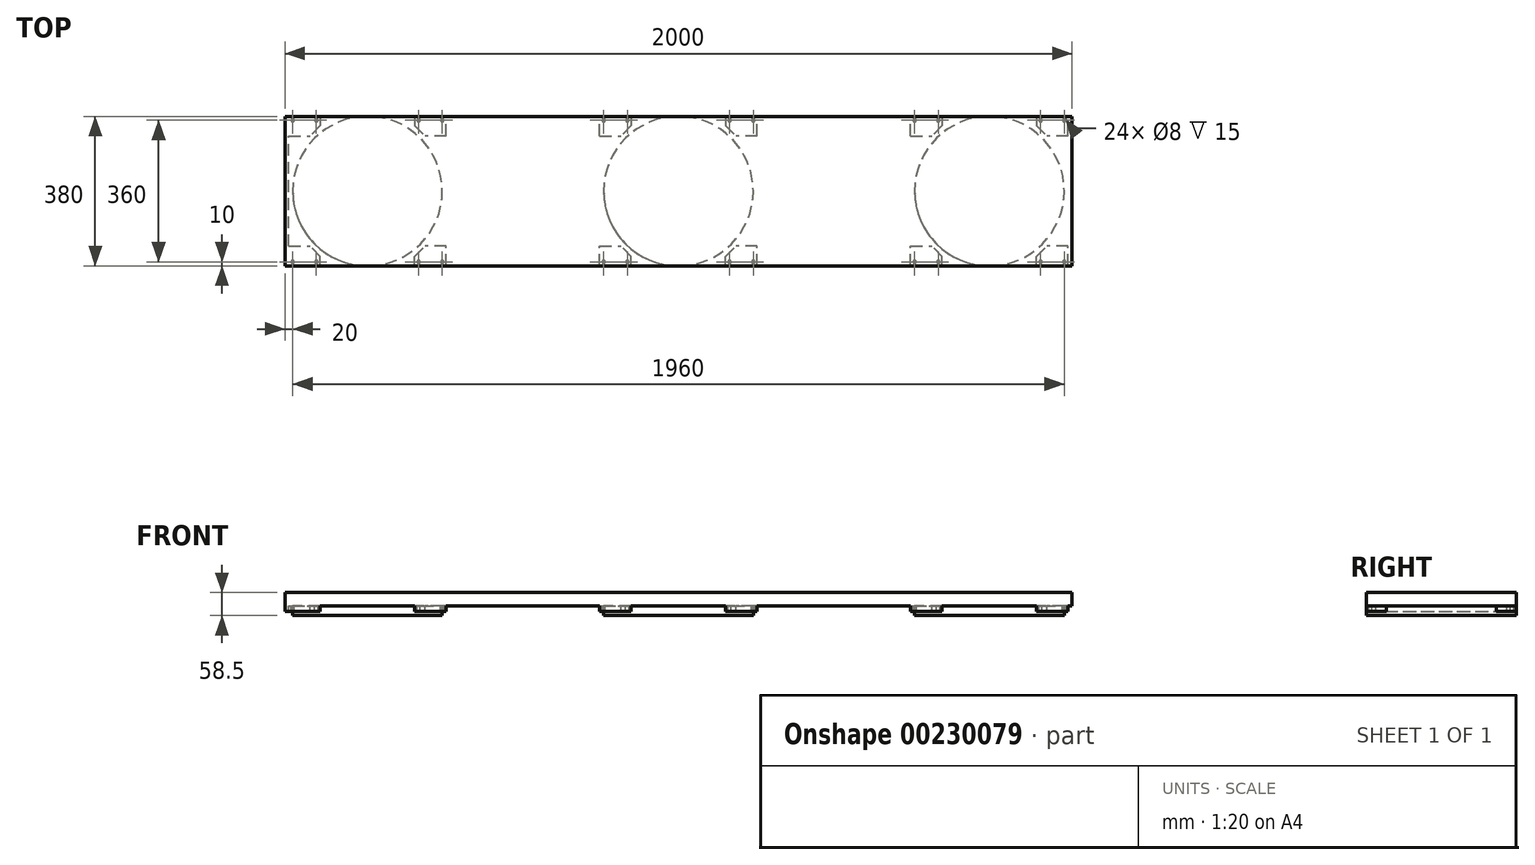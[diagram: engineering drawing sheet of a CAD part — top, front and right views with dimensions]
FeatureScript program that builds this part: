
annotation { "Feature Type Name" : "Feature", "Feature Type Description" : "" }
export const myFeature = defineFeature(function(context is Context, id is Id, definition is map)
    precondition{}
    {
        {
            var Q0;
            Q0=qCreatedBy(makeId("Right.planeOp"),FACE);
            var sketch = newSketch(context, id + "F0", { "sketchPlane" : qUnion([Q0])});
            skLineSegment(sketch, "E0.bottom", {"start": v(-190, 0) * mm, "end": v(190, 0) * mm});
            skLineSegment(sketch, "E0.top", {"start": v(-190, 33.5) * mm, "end": v(190, 33.5) * mm});
            skLineSegment(sketch, "E0.left", {"start": v(-190, 0) * mm, "end": v(-190, 33.5) * mm});
            skLineSegment(sketch, "E0.right", {"start": v(190, 0) * mm, "end": v(190, 33.5) * mm});
            skSolve(sketch);
        }
        {
            var Q0;
            Q0=makeQuery(id+"F0.imprint","IMPRINT",FACE,{"disambiguationData":[TD([[makeQuery(id+"F0.imprint","IMPRINT",EDGE,{"derivedFrom":sQuery(id+"F0.wireOp",EDGE,"E0.bottom")}),1.0]])]});
            extrude(context, id + "F1", {"entities" : qUnion([Q0]), "endBound" : BoundingType.SYMMETRIC, "depth" : 2000 * mm});
        }
        {
            var Q0;
            Q0=makeQuery(id+"F1.opExtrude","SWEPT_FACE",FACE,{"disambiguationData":[OSD([sQuery(id+"F0.wireOp",EDGE,"E0.bottom")])]});
            var sketch = newSketch(context, id + "F2", { "sketchPlane" : qUnion([Q0])});
            skCircle(sketch, "E1", {"center": v(-790, 0) * mm, "radius": 190 * mm});
            skCircle(sketch, "E2", {"center": v(0, 0) * mm, "radius": 190 * mm});
            skCircle(sketch, "E3", {"center": v(790, 0) * mm, "radius": 190 * mm});
            skLineSegment(sketch, "E4", {"start": v(-790, 0) * mm, "end": v(-790, 348.57) * mm, "construction": true});
            skSolve(sketch);
        }
        {
            var Q0;
            Q0=makeQuery(id+"F2.imprint","IMPRINT",FACE,{"disambiguationData":[TD([[makeQuery(id+"F2.imprint","IMPRINT",EDGE,{"derivedFrom":sQuery(id+"F2.wireOp",EDGE,"E1")}),1.0]])]});
            var Q1;
            Q1=makeQuery(id+"F2.imprint","IMPRINT",FACE,{"disambiguationData":[TD([[makeQuery(id+"F2.imprint","IMPRINT",EDGE,{"derivedFrom":sQuery(id+"F2.wireOp",EDGE,"E2")}),1.0]])]});
            var Q2;
            Q2=makeQuery(id+"F2.imprint","IMPRINT",FACE,{"disambiguationData":[TD([[makeQuery(id+"F2.imprint","IMPRINT",EDGE,{"derivedFrom":sQuery(id+"F2.wireOp",EDGE,"E3")}),1.0]])]});
            extrude(context, id + "F3", {"entities" : qUnion([Q0, Q1, Q2]), "operationType" : NewBodyOperationType.ADD, "depth" : 25 * mm});
        }
        {
            var Q0;
            {var subQ1=sQuery(id+"F0.wireOp",EDGE,"E0.left");var subQ3=sQuery(id+"F0.wireOp",EDGE,"E0.bottom");Q0=makeQuery(id+"F3.boolean.opBoolean","SPLIT",FACE,{"disambiguationData":[TD([makeQuery(id+"F1.opExtrude","SWEPT_FACE",FACE,{"disambiguationData":[OSD([subQ1])]})])],"derivedFrom":makeQuery(id+"F1.opExtrude","SWEPT_FACE",FACE,{"disambiguationData":[OSD([subQ3])]})});}
            var sketch = newSketch(context, id + "F4", { "sketchPlane" : qUnion([Q0])});
            skLineSegment(sketch, "E5", {"start": v(-1000, 190) * mm, "end": v(-1000, 70) * mm});
            skLineSegment(sketch, "E6.MirrorCS", {"start": v(1000, 190) * mm, "end": v(1000, 70) * mm});
            skLineSegment(sketch, "E7.MirrorCS", {"start": v(1000, -70) * mm, "end": v(1000, -195) * mm});
            skLineSegment(sketch, "E8", {"start": v(-1000, 70) * mm, "end": v(1000, 70) * mm, "construction": true});
            skLineSegment(sketch, "E9", {"start": v(1000, -70) * mm, "end": v(-1000, -70) * mm, "construction": true});
            skLineSegment(sketch, "E10", {"start": v(-990, 190) * mm, "end": v(-990, -190) * mm});
            skLineSegment(sketch, "E11.MirrorCS", {"start": v(990, 190) * mm, "end": v(990, -190) * mm});
            skLineSegment(sketch, "E12.bottom", {"start": v(-990, 190) * mm, "end": v(-910, 190) * mm});
            skLineSegment(sketch, "E12.top", {"start": v(-990, 140) * mm, "end": v(-935.72, 140) * mm});
            skLineSegment(sketch, "E12.left", {"start": v(-990, 190) * mm, "end": v(-990, 140) * mm});
            skLineSegment(sketch, "E12.right", {"start": v(-910, 190) * mm, "end": v(-910, 166.15) * mm});
            skLineSegment(sketch, "E13", {"start": v(-910, 166.15) * mm, "end": v(-935.72, 140) * mm});
            skLineSegment(sketch, "E14.MirrorCS", {"start": v(-990, -140) * mm, "end": v(-935.72, -140) * mm});
            skLineSegment(sketch, "E15.MirrorCS", {"start": v(-910, -166.15) * mm, "end": v(-935.72, -140) * mm});
            skLineSegment(sketch, "E16.MirrorCS", {"start": v(-910, -190) * mm, "end": v(-910, -166.15) * mm});
            skLineSegment(sketch, "E17.MirrorCS", {"start": v(-990, -190) * mm, "end": v(-910, -190) * mm});
            skLineSegment(sketch, "E18.MirrorCS", {"start": v(990, 140) * mm, "end": v(935.72, 140) * mm});
            skLineSegment(sketch, "E19.MirrorCS", {"start": v(910, 166.15) * mm, "end": v(935.72, 140) * mm});
            skLineSegment(sketch, "E20.MirrorCS", {"start": v(910, 190) * mm, "end": v(910, 166.15) * mm});
            skLineSegment(sketch, "E21.MirrorCS", {"start": v(990, 190) * mm, "end": v(910, 190) * mm});
            skLineSegment(sketch, "E22.MirrorCS", {"start": v(990, -140) * mm, "end": v(935.72, -140) * mm});
            skLineSegment(sketch, "E23.MirrorCS", {"start": v(910, -166.15) * mm, "end": v(935.72, -140) * mm});
            skLineSegment(sketch, "E24.MirrorCS", {"start": v(910, -190) * mm, "end": v(910, -166.15) * mm});
            skLineSegment(sketch, "E25.MirrorCS", {"start": v(990, -190) * mm, "end": v(910, -190) * mm});
            skCircle(sketch, "E26", {"center": v(-980, 180) * mm, "radius": 4 * mm});
            skPoint(sketch, "E26.centerSnap0", {"position": v(-990, 165) * mm});
            skCircle(sketch, "E27", {"center": v(-920, 180) * mm, "radius": 4 * mm});
            skCircle(sketch, "E28.MirrorC", {"center": v(-920, -180) * mm, "radius": 4 * mm});
            skCircle(sketch, "E29.MirrorC", {"center": v(-980, -180) * mm, "radius": 4 * mm});
            skCircle(sketch, "E30.MirrorC", {"center": v(920, 180) * mm, "radius": 4 * mm});
            skCircle(sketch, "E31.MirrorC", {"center": v(980, 180) * mm, "radius": 4 * mm});
            skCircle(sketch, "E32.MirrorC", {"center": v(920, -180) * mm, "radius": 4 * mm});
            skCircle(sketch, "E33.MirrorC", {"center": v(980, -180) * mm, "radius": 4 * mm});
            skLineSegment(sketch, "E34", {"start": v(-588.08, 190) * mm, "end": v(-588.08, -190) * mm});
            skLineSegment(sketch, "E35", {"start": v(-790, 190) * mm, "end": v(-790, -190) * mm, "construction": true});
            skLineSegment(sketch, "E36.MirrorCS", {"start": v(-670, 166.15) * mm, "end": v(-644.28, 140) * mm});
            skLineSegment(sketch, "E37.MirrorCS", {"start": v(-590, 140) * mm, "end": v(-644.28, 140) * mm});
            skLineSegment(sketch, "E38.MirrorCS", {"start": v(-670, 190) * mm, "end": v(-670, 166.15) * mm});
            skLineSegment(sketch, "E39.MirrorCS", {"start": v(-590, 190) * mm, "end": v(-670, 190) * mm});
            skLineSegment(sketch, "E40.MirrorCS", {"start": v(-590, 190) * mm, "end": v(-590, 140) * mm});
            skCircle(sketch, "E41.MirrorC", {"center": v(-600, 180) * mm, "radius": 4 * mm});
            skCircle(sketch, "E42.MirrorC", {"center": v(-660, 180) * mm, "radius": 4 * mm});
            skLineSegment(sketch, "E43.MirrorCS", {"start": v(-670, -166.15) * mm, "end": v(-644.28, -140) * mm});
            skLineSegment(sketch, "E44.MirrorCS", {"start": v(-670, -190) * mm, "end": v(-670, -166.15) * mm});
            skLineSegment(sketch, "E45.MirrorCS", {"start": v(-590, -140) * mm, "end": v(-644.28, -140) * mm});
            skLineSegment(sketch, "E46.MirrorCS", {"start": v(-590, 190) * mm, "end": v(-590, -190) * mm});
            skLineSegment(sketch, "E47.MirrorCS", {"start": v(-590, -190) * mm, "end": v(-670, -190) * mm});
            skCircle(sketch, "E48.MirrorC", {"center": v(-660, -180) * mm, "radius": 4 * mm});
            skCircle(sketch, "E49.MirrorC", {"center": v(-600, -180) * mm, "radius": 4 * mm});
            skLineSegment(sketch, "E50.MirrorCS", {"start": v(590, 140) * mm, "end": v(644.28, 140) * mm});
            skLineSegment(sketch, "E51.MirrorCS", {"start": v(670, 166.15) * mm, "end": v(644.28, 140) * mm});
            skLineSegment(sketch, "E52.MirrorCS", {"start": v(670, 190) * mm, "end": v(670, 166.15) * mm});
            skLineSegment(sketch, "E53.MirrorCS", {"start": v(590, 190) * mm, "end": v(670, 190) * mm});
            skLineSegment(sketch, "E54.MirrorCS", {"start": v(590, 190) * mm, "end": v(590, -190) * mm});
            skCircle(sketch, "E55.MirrorC", {"center": v(600, 180) * mm, "radius": 4 * mm});
            skCircle(sketch, "E56.MirrorC", {"center": v(660, 180) * mm, "radius": 4 * mm});
            skLineSegment(sketch, "E57.MirrorCS", {"start": v(670, -166.15) * mm, "end": v(644.28, -140) * mm});
            skLineSegment(sketch, "E58.MirrorCS", {"start": v(590, -140) * mm, "end": v(644.28, -140) * mm});
            skLineSegment(sketch, "E59.MirrorCS", {"start": v(670, -190) * mm, "end": v(670, -166.15) * mm});
            skLineSegment(sketch, "E60.MirrorCS", {"start": v(590, -190) * mm, "end": v(670, -190) * mm});
            skCircle(sketch, "E61.MirrorC", {"center": v(600, -180) * mm, "radius": 4 * mm});
            skCircle(sketch, "E62.MirrorC", {"center": v(660, -180) * mm, "radius": 4 * mm});
            skLineSegment(sketch, "E63", {"start": v(-790, 0) * mm, "end": v(0, 0) * mm, "construction": true});
            skLineSegment(sketch, "E64", {"start": v(-395, 0) * mm, "end": v(-395, 311.98) * mm, "construction": true});
            skLineSegment(sketch, "E65.MirrorCS", {"start": v(-120, 166.15) * mm, "end": v(-145.72, 140) * mm});
            skLineSegment(sketch, "E66.MirrorCS", {"start": v(-120, 190) * mm, "end": v(-120, 166.15) * mm});
            skCircle(sketch, "E67.MirrorC", {"center": v(-130, 180) * mm, "radius": 4 * mm});
            skCircle(sketch, "E68.MirrorC", {"center": v(-190, 180) * mm, "radius": 4 * mm});
            skLineSegment(sketch, "E69.MirrorCS", {"start": v(-200, 190) * mm, "end": v(-200, 140) * mm});
            skLineSegment(sketch, "E70.MirrorCS", {"start": v(-200, 140) * mm, "end": v(-145.72, 140) * mm});
            skLineSegment(sketch, "E71.MirrorCS", {"start": v(-200, 190) * mm, "end": v(-120, 190) * mm});
            skLineSegment(sketch, "E72.MirrorCS", {"start": v(120, 190) * mm, "end": v(120, 166.15) * mm});
            skLineSegment(sketch, "E73.MirrorCS", {"start": v(120, -190) * mm, "end": v(120, -166.15) * mm});
            skLineSegment(sketch, "E74.MirrorCS", {"start": v(120, 166.15) * mm, "end": v(145.72, 140) * mm});
            skLineSegment(sketch, "E75.MirrorCS", {"start": v(200, 190) * mm, "end": v(200, 140) * mm});
            skCircle(sketch, "E76.MirrorC", {"center": v(130, 180) * mm, "radius": 4 * mm});
            skLineSegment(sketch, "E77.MirrorCS", {"start": v(200, 190) * mm, "end": v(120, 190) * mm});
            skCircle(sketch, "E78.MirrorC", {"center": v(190, 180) * mm, "radius": 4 * mm});
            skCircle(sketch, "E79.MirrorC", {"center": v(190, -180) * mm, "radius": 4 * mm});
            skCircle(sketch, "E80.MirrorC", {"center": v(130, -180) * mm, "radius": 4 * mm});
            skLineSegment(sketch, "E81.MirrorCS", {"start": v(200, -190) * mm, "end": v(120, -190) * mm});
            skLineSegment(sketch, "E82.MirrorCS", {"start": v(120, -166.15) * mm, "end": v(145.72, -140) * mm});
            skLineSegment(sketch, "E83.MirrorCS", {"start": v(210, 190) * mm, "end": v(210, 70) * mm});
            skLineSegment(sketch, "E84.MirrorCS", {"start": v(200, 190) * mm, "end": v(200, -190) * mm});
            skPoint(sketch, "E85.MirrorP", {"position": v(200, 165) * mm});
            skLineSegment(sketch, "E86.MirrorCS", {"start": v(200, 140) * mm, "end": v(145.72, 140) * mm});
            skLineSegment(sketch, "E87.MirrorCS", {"start": v(200, -140) * mm, "end": v(145.72, -140) * mm});
            skLineSegment(sketch, "E88.MirrorCS", {"start": v(-120, -190) * mm, "end": v(-120, -166.15) * mm});
            skCircle(sketch, "E89.MirrorC", {"center": v(-130, -180) * mm, "radius": 4 * mm});
            skCircle(sketch, "E90.MirrorC", {"center": v(-190, -180) * mm, "radius": 4 * mm});
            skLineSegment(sketch, "E91.MirrorCS", {"start": v(-200, -140) * mm, "end": v(-145.72, -140) * mm});
            skLineSegment(sketch, "E92.MirrorCS", {"start": v(-200, -190) * mm, "end": v(-120, -190) * mm});
            skLineSegment(sketch, "E93.MirrorCS", {"start": v(-120, -166.15) * mm, "end": v(-145.72, -140) * mm});
            skLineSegment(sketch, "E94.MirrorCS", {"start": v(-200, 190) * mm, "end": v(-200, -190) * mm});
            skSolve(sketch);
        }
        {
            var Q0;
            Q0 = qSketchRegion(id + "F4", true);
            var Q1;
            {var subQ0=sQuery(id+"F4.wireOp",EDGE,"7qvQ77yO-Eq50-rJ66-5xp7-DA5szfmi9L9O");var subQ3=sQuery(id+"F4.wireOp",EDGE,"E10");var subQ4=makeQuery(id+"F4.imprint","INTERSECT",VERTEX,{"derivedFrom":[subQ0,subQ3]});Q1=makeQuery(id+"F4.imprint","IMPRINT",FACE,{"disambiguationData":[TD([[makeQuery(id+"F4.imprint","IMPRINT",EDGE,{"disambiguationData":[TD([[subQ4,-1.0]])],"derivedFrom":subQ3}),-1.0]])]});}
            var Q2;
            {var subQ0=sQuery(id+"F4.wireOp",EDGE,"429b1110-2f48-4ad4-b680-34f3e81fc5a90.MirrorCS");var subQ3=sQuery(id+"F4.wireOp",EDGE,"E11.MirrorCS");var subQ4=makeQuery(id+"F4.imprint","INTERSECT",VERTEX,{"derivedFrom":[subQ0,subQ3]});Q2=makeQuery(id+"F4.imprint","IMPRINT",FACE,{"disambiguationData":[TD([[makeQuery(id+"F4.imprint","IMPRINT",EDGE,{"disambiguationData":[TD([[subQ4,-1.0]])],"derivedFrom":subQ3}),1.0]])]});}
            extrude(context, id + "F5", {"entities" : qUnion([Q0, Q1, Q2]), "operationType" : NewBodyOperationType.ADD, "depth" : 15 * mm});
        }
    });
